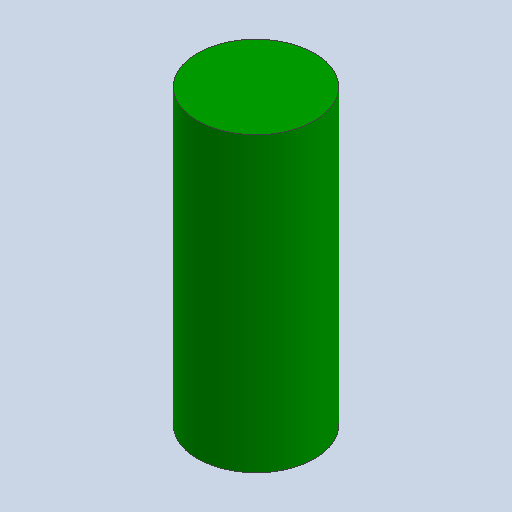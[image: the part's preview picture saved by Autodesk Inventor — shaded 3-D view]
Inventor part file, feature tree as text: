
AUTODESK INVENTOR PART (.ipt)
format: ipt  version: 2025.2 (Build 292293000, 293)  size: 89,600 bytes
history: native  units: in
note: dims shown in document units (in); Inventor stores cm internally (conversion verified against a paired STEP export)
features: other x3, sketch x1
ambient origin geometry x8: Origin, YZ Plane, XZ Plane, XY Plane, X Axis, Y Axis, Z Axis, Center Point
bodies: Solid1 (feature_tree)
feature tree (4):
  other  "26650(Green)_MIR4.ipt"
  other  "Solid1::26650(Green)_MIR4.ipt"
  other  "TaggingFeature1"
  sketch  "Sketch1"  dims[d0=0.3937in]
